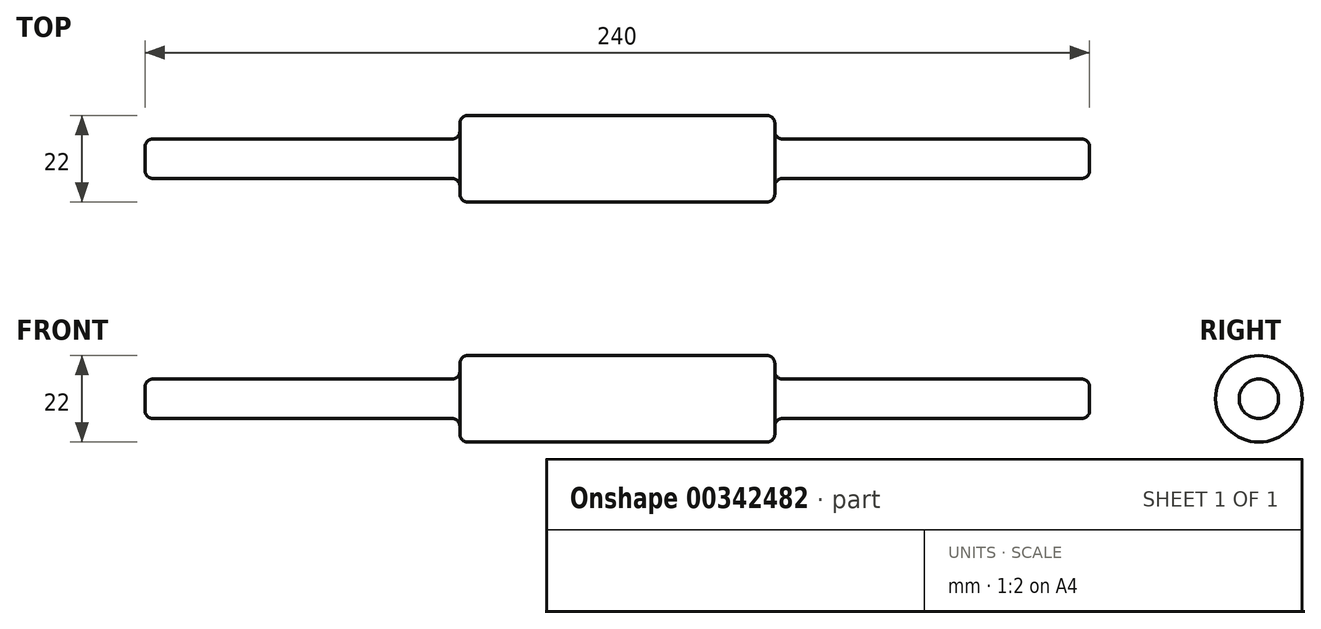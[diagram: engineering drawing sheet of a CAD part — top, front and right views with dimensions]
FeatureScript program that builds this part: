
annotation { "Feature Type Name" : "Feature", "Feature Type Description" : "" }
export const myFeature = defineFeature(function(context is Context, id is Id, definition is map)
    precondition{}
    {
        {
            var Q0;
            Q0=qCreatedBy(makeId("Right.planeOp"),FACE);
            var sketch = newSketch(context, id + "F0", { "sketchPlane" : qUnion([Q0])});
            skCircle(sketch, "E0", {"center": v(0, 0) * mm, "radius": 11 * mm});
            skCircle(sketch, "E1", {"center": v(0, 0) * mm, "radius": 5 * mm});
            skSolve(sketch);
        }
        {
            var Q0;
            Q0=makeQuery(id+"F0.imprint","IMPRINT",FACE,{"disambiguationData":[TD([[makeQuery(id+"F0.imprint","IMPRINT",EDGE,{"derivedFrom":sQuery(id+"F0.wireOp",EDGE,"E0")}),1.0]])]});
            var Q1;
            Q1=makeQuery(id+"F0.imprint","IMPRINT",FACE,{"disambiguationData":[TD([[makeQuery(id+"F0.imprint","IMPRINT",EDGE,{"derivedFrom":sQuery(id+"F0.wireOp",EDGE,"E1")}),1.0]])]});
            extrude(context, id + "F1", {"entities" : qUnion([Q0, Q1]), "depth" : 80 * mm, "symmetric" : true});
        }
        {
            var Q0;
            Q0=makeQuery(id+"F0.imprint","IMPRINT",FACE,{"disambiguationData":[TD([[makeQuery(id+"F0.imprint","IMPRINT",EDGE,{"derivedFrom":sQuery(id+"F0.wireOp",EDGE,"E1")}),1.0]])]});
            extrude(context, id + "F2", {"entities" : qUnion([Q0]), "operationType" : NewBodyOperationType.ADD, "depth" : 240 * mm, "symmetric" : true});
        }
        {
            var Q0;
            Q0=makeQuery(id+"F1.opExtrude","CAP_FACE",FACE,{"disambiguationData":[OSD([sQuery(id+"F0.wireOp",EDGE,"E0")])],"isStart":true});
            var Q1;
            Q1=makeQuery(id+"F1.opExtrude","CAP_FACE",FACE,{"disambiguationData":[OSD([sQuery(id+"F0.wireOp",EDGE,"E0")])],"isStart":false});
            var Q2;
            Q2=makeQuery(id+"F2.opExtrude","CAP_FACE",FACE,{"disambiguationData":[OSD([sQuery(id+"F0.wireOp",EDGE,"E1")])],"isStart":false});
            var Q3;
            Q3=makeQuery(id+"F2.opExtrude","CAP_EDGE",EDGE,{"disambiguationData":[OSD([sQuery(id+"F0.wireOp",EDGE,"E1")])],"isStart":true});
            fillet(context, id + "F3", {"entities" : qUnion([Q0, Q1, Q2, Q3]), "radius" : 2 * mm, "tangentPropagation" : true, "allowEdgeOverflow" : false});
        }
    });
